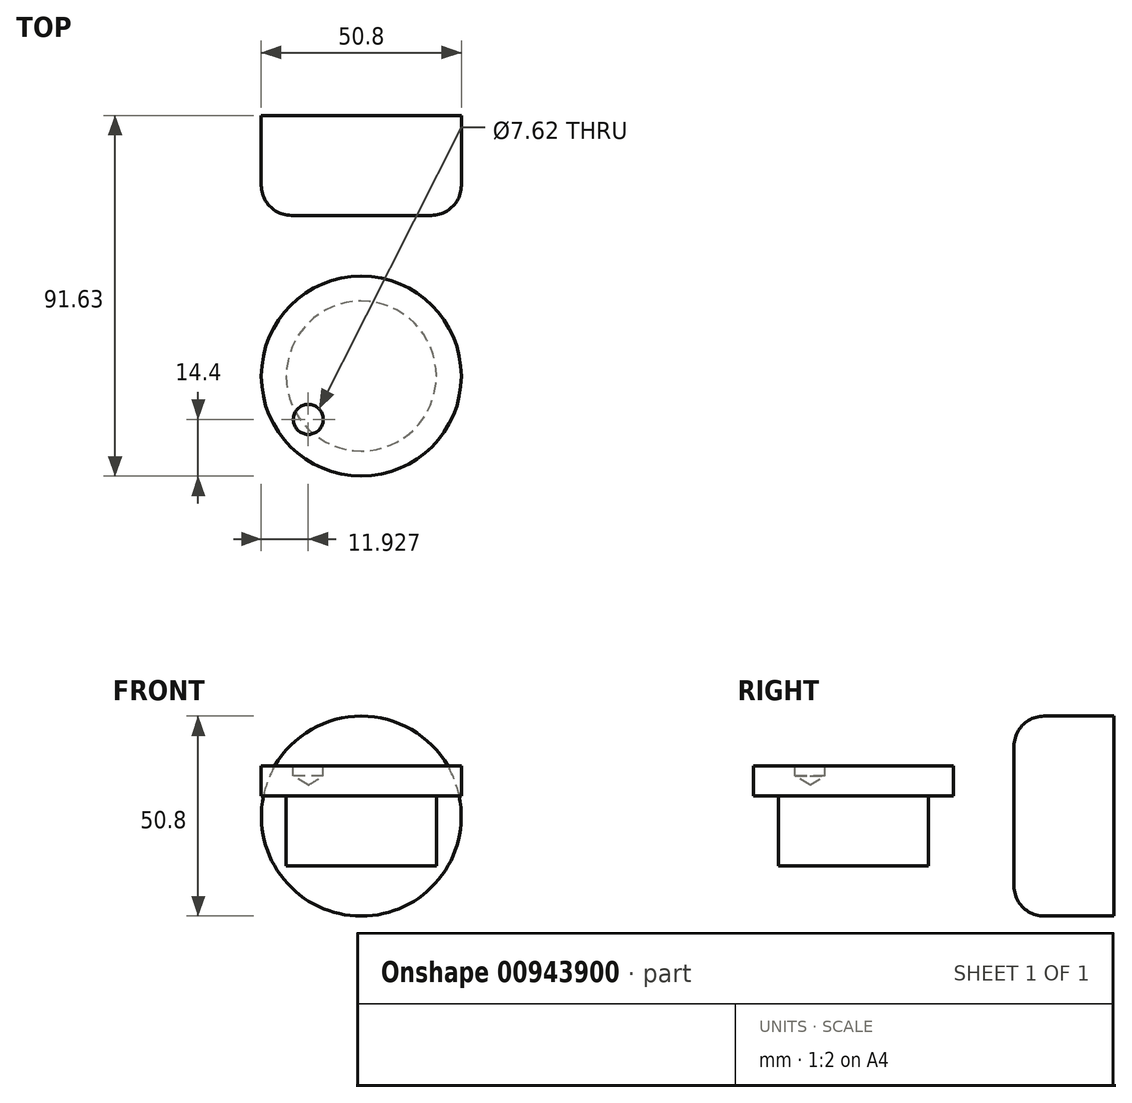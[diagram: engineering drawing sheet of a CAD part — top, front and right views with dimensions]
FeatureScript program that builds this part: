
annotation { "Feature Type Name" : "Feature", "Feature Type Description" : "" }
export const myFeature = defineFeature(function(context is Context, id is Id, definition is map)
    precondition{}
    {
        {
            var Q0;
            Q0=qCreatedBy(makeId("Front.planeOp"),FACE);
            var sketch = newSketch(context, id + "F0", { "sketchPlane" : qUnion([Q0])});
            skCircle(sketch, "E0", {"center": v(0, 0) * mm, "radius": 25.4 * mm});
            skSolve(sketch);
        }
        {
            var Q0;
            Q0 = qSketchRegion(id + "F0", true);
            extrude(context, id + "F1", {"entities" : qUnion([Q0]), "oppositeDirection" : true, "depth" : 25.4 * mm, "offsetDistance" : 25.4 * mm});
        }
        {
            var Q0;
            Q0=makeQuery(id+"F1.opExtrude","CAP_EDGE",EDGE,{"disambiguationData":[OSD([sQuery(id+"F0.wireOp",EDGE,"E0")])],"isStart":true});
            fillet(context, id + "F2", {"entities" : qUnion([Q0]), "radius" : 7.62 * mm, "tangentPropagation" : true, "allowEdgeOverflow" : false});
        }
        {
            var Q0;
            Q0=qCreatedBy(makeId("Top.planeOp"),FACE);
            var sketch = newSketch(context, id + "F3", { "sketchPlane" : qUnion([Q0])});
            skCircle(sketch, "E1", {"center": v(0, -40.83) * mm, "radius": 19.05 * mm});
            skSolve(sketch);
        }
        {
            var Q0;
            Q0=makeQuery(id+"F3.imprint","IMPRINT",FACE,{"disambiguationData":[TD([[makeQuery(id+"F3.imprint","IMPRINT",EDGE,{"derivedFrom":sQuery(id+"F3.wireOp",EDGE,"E1")}),1.0]])]});
            var Q1;
            Q1=sQuery(id+"F3.wireOp",EDGE,"E1");
            extrude(context, id + "F4", {"entities" : qUnion([Q0]), "surfaceEntities" : qUnion([Q1]), "endBound" : BoundingType.SYMMETRIC, "depth" : 25.4 * mm, "offsetDistance" : 25.4 * mm});
        }
        {
            var Q0;
            Q0=makeQuery(id+"F4.opExtrude","CAP_FACE",FACE,{"disambiguationData":[OSD([sQuery(id+"F3.wireOp",EDGE,"E1")])],"isStart":false});
            var sketch = newSketch(context, id + "F5", { "sketchPlane" : qUnion([Q0])});
            skCircle(sketch, "E2", {"center": v(0, -40.83) * mm, "radius": 25.4 * mm});
            skSolve(sketch);
        }
        {
            var Q0;
            Q0=makeQuery(id+"F5.imprint","IMPRINT",FACE,{"disambiguationData":[TD([[makeQuery(id+"F5.imprint","IMPRINT",EDGE,{"derivedFrom":sQuery(id+"F5.wireOp",EDGE,"E2")}),1.0]])]});
            var Q1;
            Q1=sQuery(id+"F5.wireOp",EDGE,"E2");
            extrude(context, id + "F6", {"entities" : qUnion([Q0]), "operationType" : NewBodyOperationType.ADD, "surfaceEntities" : qUnion([Q1]), "oppositeDirection" : true, "depth" : 7.62 * mm, "offsetDistance" : 25.4 * mm});
        }
        {
            var Q0;
            {var subQ0=sQuery(id+"F3.wireOp",EDGE,"E1");Q0=makeQuery(id+"F6.boolean.opBoolean","MERGE",FACE,{"derivedFrom":[makeQuery(id+"F4.opExtrude","CAP_FACE",FACE,{"disambiguationData":[OSD([subQ0])],"isStart":false}),makeQuery(id+"F6.opExtrude","CAP_FACE",FACE,{"disambiguationData":[OSD([subQ0,sQuery(id+"F5.wireOp",EDGE,"E2")])],"isStart":true})]});}
            var sketch = newSketch(context, id + "F7", { "sketchPlane" : qUnion([Q0])});
            skCircle(sketch, "E3", {"center": v(-13.47, -51.83) * mm, "radius": 2.85 * mm});
            skSolve(sketch);
        }
        {
            var Q0;
            Q0=sQuery(id+"F7.wireOp",VERTEX,"E3.center");
            var Q1;
            Q1=makeQuery(id+"F4.opExtrude","SWEPT_BODY",BODY,{"disambiguationData":[OSD([sQuery(id+"F3.wireOp",EDGE,"E1")])]});
            hole(context, id + "F8", {"style" : HoleStyle.SIMPLE, "endStyle" : HoleEndStyle.BLIND, "holeDiameter" : 7.62 * mm, "majorDiameter" : 6.35 * mm, "holeDepth" : 2.54 * mm, "isTappedThrough" : true, "tappedDepth" : 12.7 * mm, "tapClearance" : 3, "locations" : qUnion([Q0]), "scope" : qUnion([Q1])});
        }
    });
